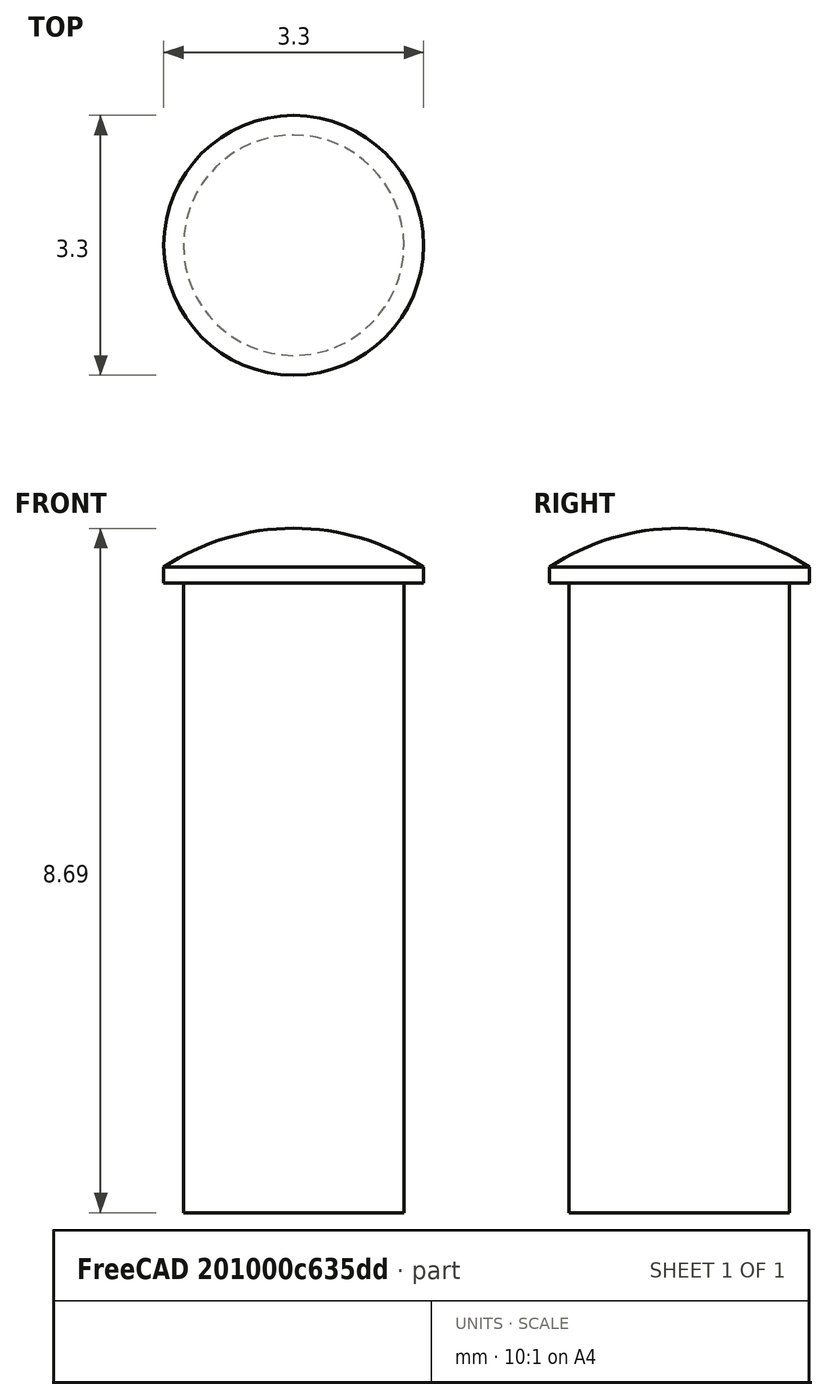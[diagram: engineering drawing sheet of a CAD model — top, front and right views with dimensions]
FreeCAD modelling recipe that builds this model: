
FCSTD DOCUMENT  (FreeCAD 1.0R39319 (Git))
Label: PLASTIC-LIGHTPIPE
License: All rights reserved
LicenseURL: http://en.wikipedia.org/wiki/All_rights_reserved
objects: Sketcher::SketchObject×1, PartDesign::Revolution×1, PartDesign::CoordinateSystem×1, PartDesign::Body×1
note: 7 computed .brp shape members not serialized (recipe doc carries the construction recipe); baked Part::Feature solids carry a one-line shape summary decoded from their .brp

FEATURE [Sketcher::SketchObject] Sketch
  ArcFitTolerance = 0
  AttachmentSupport = -> [XZ_Plane]
  FullyConstrained = true
  MakeInternals = false
  MapMode = 5
  Placement = pos=(0,0,0) rot=(1,0,0;1.5708rad)
  expr: Constraints[4] = 2.8 / 2
  sketch-geometry (6):
    g0: LineSegment StartX=-1.4 StartY=0 StartZ=0 EndX=-1.4 EndY=-8 EndZ=0
    g1: LineSegment StartX=-1.4 StartY=-8 StartZ=0 EndX=0 EndY=-8 EndZ=0
    g2: LineSegment StartX=-1.65 StartY=0 StartZ=0 EndX=-1.65 EndY=0.2 EndZ=0
    g3: ArcOfCircle CenterX=0 CenterY=-2.30549 CenterZ=0 NormalX=0 NormalY=0 NormalZ=1 AngleXU=0 Radius=3 StartAngle=1.5708 EndAngle=2.15316
    g4: LineSegment StartX=2e-16 StartY=0.694506 StartZ=0 EndX=0 EndY=-8 EndZ=0
    g5: LineSegment StartX=-1.65 StartY=0 StartZ=0 EndX=-1.4 EndY=0 EndZ=0
  constraints (20):
    c: Vertical(g0)
    c: Coincident(g0,g1)
    c: PointOnObject(g1,g-2)
    c: Horizontal(g1)
    c: DistanceX(g1,g1) = 1.4
    c: Vertical(g2)
    c: PointOnObject(g3,g-2)
    c: PointOnObject(g3,g-2)
    c: Coincident(g3,g2)
    c: DistanceX(g2,g-1) = 1.65
    c: Radius(g3) = 3
    c: Coincident(g4,g3)
    c: Coincident(g4,g1)
    c: Coincident(g5,g2)
    c: Coincident(g5,g0)
    c: Horizontal(g5)
    c: DistanceY(g2,g2) = 0.2
    c: PointOnObject(g0,g-1)
    c: DistanceY(g0,g0) = 8
    c: DistanceY(g2,g3) = 0.694506
FEATURE [PartDesign::Revolution] Revolution
  Angle = 360
  Angle2 = 60
  Axis = (0,2e-16,1)
  Base = (0,0,0)
  Placement = pos=(0,0,0) rot=(1,0,0;1.5708rad)
  Profile = -> Sketch
  ReferenceAxis = -> Sketch [V_Axis]
  Suppressed = false
  Type = 0
FEATURE [PartDesign::CoordinateSystem] LCS_1
  AttacherType = Attacher::AttachEngine3D
FEATURE [PartDesign::Body] Body  label="PLASTIC-LIGHTPIPE"
  AllowCompound = false
  Group = -> [Sketch,Revolution,LCS_1]
  Origin = -> Origin
  Tip = -> Revolution
